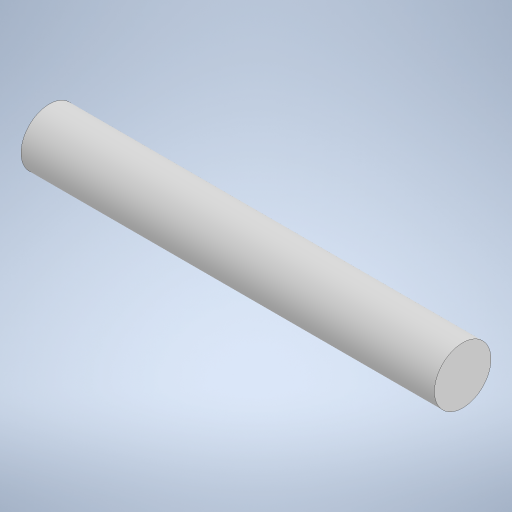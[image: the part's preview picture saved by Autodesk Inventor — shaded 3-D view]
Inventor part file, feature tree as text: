
AUTODESK INVENTOR PART (.ipt)
format: ipt  version: 2023 (Build 270158030, 158C)  size: 222,208 bytes
history: native  units: mm
features: extrude x1, sketch x1
ambient origin geometry x8: Origin, YZ Plane, XZ Plane, XY Plane, X Axis, Y Axis, Z Axis, Center Point
bodies: Solid1 (feature_tree)
feature tree (2):
  extrude  "Extrusion1"  Depth=13.9mm TaperAngle=0.0deg
  sketch  "Sketch1"  dims[d0=1.9mm d1=13.9mm d2=0.0mm]
